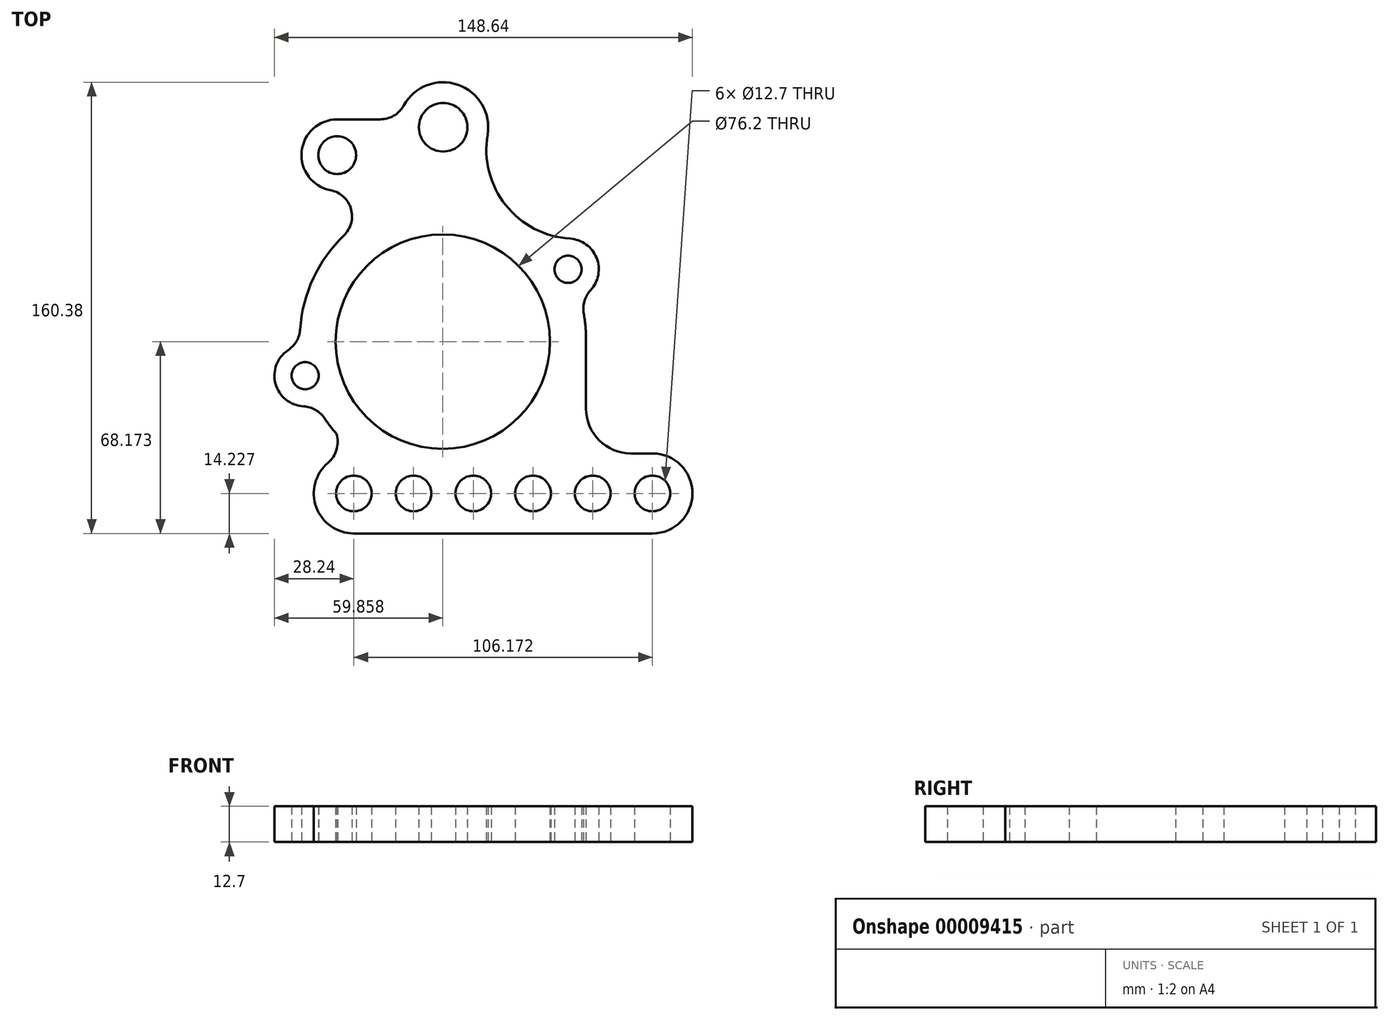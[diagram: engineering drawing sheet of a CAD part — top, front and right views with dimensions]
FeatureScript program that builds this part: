
annotation { "Feature Type Name" : "Feature", "Feature Type Description" : "" }
export const myFeature = defineFeature(function(context is Context, id is Id, definition is map)
    precondition{}
    {
        {
            var Q0;
            Q0=qCreatedBy(makeId("Top.planeOp"),FACE);
            var sketch = newSketch(context, id + "F0", { "sketchPlane" : qUnion([Q0])});
            skCircle(sketch, "E0", {"center": v(-31.75, -55) * mm, "radius": 6.35 * mm});
            skCircle(sketch, "E1.1.0.0", {"center": v(-10.52, -55) * mm, "radius": 6.35 * mm});
            skCircle(sketch, "E1.2.0.0", {"center": v(10.72, -55) * mm, "radius": 6.35 * mm});
            skCircle(sketch, "E1.3.0.0", {"center": v(31.95, -55) * mm, "radius": 6.35 * mm});
            skCircle(sketch, "E1.4.0.0", {"center": v(53.19, -55) * mm, "radius": 6.35 * mm});
            skCircle(sketch, "E1.5.0.0", {"center": v(74.42, -55) * mm, "radius": 6.35 * mm});
            skLineSegment(sketch, "E1.direction1", {"start": v(-31.75, -55) * mm, "end": v(-10.52, -55) * mm, "construction": true});
            skArc(sketch, "E2", {"start": v(74.42, -69.22) * mm, "mid": v(88.65, -55) * mm, "end": v(74.42, -40.77) * mm});
            skLineSegment(sketch, "E3", {"start": v(66.8, -40.77) * mm, "end": v(74.42, -40.77) * mm});
            skLineSegment(sketch, "E4", {"start": v(-31.75, -69.22) * mm, "end": v(74.42, -69.22) * mm});
            skArc(sketch, "E5", {"start": v(-42.34, -64.49) * mm, "mid": v(-38.66, -66.79) * mm, "end": v(-34.86, -68.87) * mm, "construction": true});
            skCircle(sketch, "E6", {"center": v(0, 0) * mm, "radius": 63.5 * mm, "construction": true});
            skArc(sketch, "E7", {"start": v(-42.18, -28.31) * mm, "mid": v(-40.19, -31.07) * mm, "end": v(-38.02, -33.7) * mm});
            skLineSegment(sketch, "E8", {"start": v(-0.13, -1.05) * mm, "end": v(109.64, 62.33) * mm, "construction": true});
            skLineSegment(sketch, "E9", {"start": v(0, 0) * mm, "end": v(-98.15, -26.3) * mm, "construction": true});
            skArc(sketch, "E10", {"start": v(-55.13, -4.06) * mm, "mid": v(-59.6, -16.03) * mm, "end": v(-49.67, -24.05) * mm});
            skArc(sketch, "E11", {"start": v(52.43, 17.25) * mm, "mid": v(53.95, 29.98) * mm, "end": v(42.33, 35.4) * mm});
            skCircle(sketch, "E12", {"center": v(-0.13, -1.05) * mm, "radius": 38.1 * mm});
            skCircle(sketch, "E13", {"center": v(-49.07, -13.15) * mm, "radius": 4.83 * mm});
            skCircle(sketch, "E14", {"center": v(44.4, 24.67) * mm, "radius": 4.83 * mm});
            skLineSegment(sketch, "E15", {"start": v(50.8, 0) * mm, "end": v(50.8, -24.77) * mm});
            skArc(sketch, "E16.filletArc", {"start": v(50.8, -24.77) * mm, "mid": v(55.49, -36.08) * mm, "end": v(66.8, -40.77) * mm});
            skArc(sketch, "E17", {"start": v(-42.18, -28.31) * mm, "mid": v(-45.42, -25.3) * mm, "end": v(-49.67, -24.05) * mm});
            skArc(sketch, "E18.trimOffspring", {"start": v(-40.94, -44.13) * mm, "mid": v(-45.1, -59.88) * mm, "end": v(-31.75, -69.22) * mm});
            skArc(sketch, "E19.trimOffspring", {"start": v(50.8, 0) * mm, "mid": v(50.6, 4.5) * mm, "end": v(50, 8.96) * mm});
            skLineSegment(sketch, "E20", {"start": v(0, 0) * mm, "end": v(-31.75, -55) * mm, "construction": true});
            skArc(sketch, "E21", {"start": v(-40.94, -44.13) * mm, "mid": v(-37.87, -39.36) * mm, "end": v(-38.02, -33.7) * mm});
            skPoint(sketch, "E22.visualSharp", {"position": v(-50.9, -2.38) * mm});
            skArc(sketch, "E22.filletArc", {"start": v(-55.13, -4.06) * mm, "mid": v(-52.12, -0.86) * mm, "end": v(-50.85, 3.34) * mm});
            skArc(sketch, "E23.trimOffspring", {"start": v(-35.3, 36.7) * mm, "mid": v(-46.2, 21.47) * mm, "end": v(-50.85, 3.34) * mm});
            skPoint(sketch, "E24.visualSharp", {"position": v(48.65, 14.6) * mm});
            skArc(sketch, "E24.filletArc", {"start": v(52.43, 17.25) * mm, "mid": v(50.24, 13.4) * mm, "end": v(50, 8.96) * mm});
            skPoint(sketch, "E25.visualSharp", {"position": v(38.11, 33.6) * mm});
            skCircle(sketch, "E26", {"center": v(0, 75.15) * mm, "radius": 8.64 * mm});
            skCircle(sketch, "E27", {"center": v(-37.68, 65.26) * mm, "radius": 6.73 * mm});
            skArc(sketch, "E28", {"start": v(15.91, 73.45) * mm, "mid": v(4.83, 90.4) * mm, "end": v(-14, 82.9) * mm});
            skArc(sketch, "E29", {"start": v(-37.68, 77.96) * mm, "mid": v(-50.32, 66.46) * mm, "end": v(-40.06, 52.79) * mm});
            skLineSegment(sketch, "E30", {"start": v(-37.68, 65.26) * mm, "end": v(0, 0) * mm, "construction": true});
            skLineSegment(sketch, "E31", {"start": v(-37.68, 77.96) * mm, "end": v(-22.4, 77.96) * mm});
            skArc(sketch, "E32.filletArc", {"start": v(-22.4, 77.96) * mm, "mid": v(-17.52, 79.29) * mm, "end": v(-14, 82.9) * mm});
            skArc(sketch, "E33.trimOffspring", {"start": v(15.91, 73.45) * mm, "mid": v(-17.84, 72.98) * mm, "end": v(-48.09, 57.99) * mm, "construction": true});
            skArc(sketch, "E34", {"start": v(-35.3, 36.7) * mm, "mid": v(-32.78, 46.2) * mm, "end": v(-40.06, 52.79) * mm});
            skPoint(sketch, "E35.orphan", {"position": v(-35.3, 52.79) * mm});
            skCircle(sketch, "E36", {"center": v(44.4, 24.67) * mm, "radius": 10.92 * mm});
            skCircle(sketch, "E37", {"center": v(0, 75.15) * mm, "radius": 16 * mm});
            skArc(sketch, "E38", {"start": v(15.78, 72.5) * mm, "mid": v(22.22, 47.52) * mm, "end": v(45.1, 35.57) * mm});
            skSolve(sketch);
        }
        {
            var Q0;
            Q0=makeQuery(id+"F0.imprint","IMPRINT",FACE,{"disambiguationData":[TD([[makeQuery(id+"F0.imprint","IMPRINT",EDGE,{"derivedFrom":sQuery(id+"F0.wireOp",EDGE,"E26")}),-1.0]])]});
            var Q1;
            Q1=makeQuery(id+"F0.imprint","IMPRINT",FACE,{"disambiguationData":[TD([[makeQuery(id+"F0.imprint","IMPRINT",EDGE,{"derivedFrom":sQuery(id+"F0.wireOp",EDGE,"E0")}),-1.0]])]});
            var Q2;
            Q2=makeQuery(id+"F0.imprint","IMPRINT",FACE,{"disambiguationData":[TD([[makeQuery(id+"F0.imprint","IMPRINT",EDGE,{"derivedFrom":sQuery(id+"F0.wireOp",EDGE,"E14")}),-1.0]])]});
            extrude(context, id + "F1", {"entities" : qUnion([Q0, Q1, Q2]), "depth" : 12.7 * mm});
        }
    });
